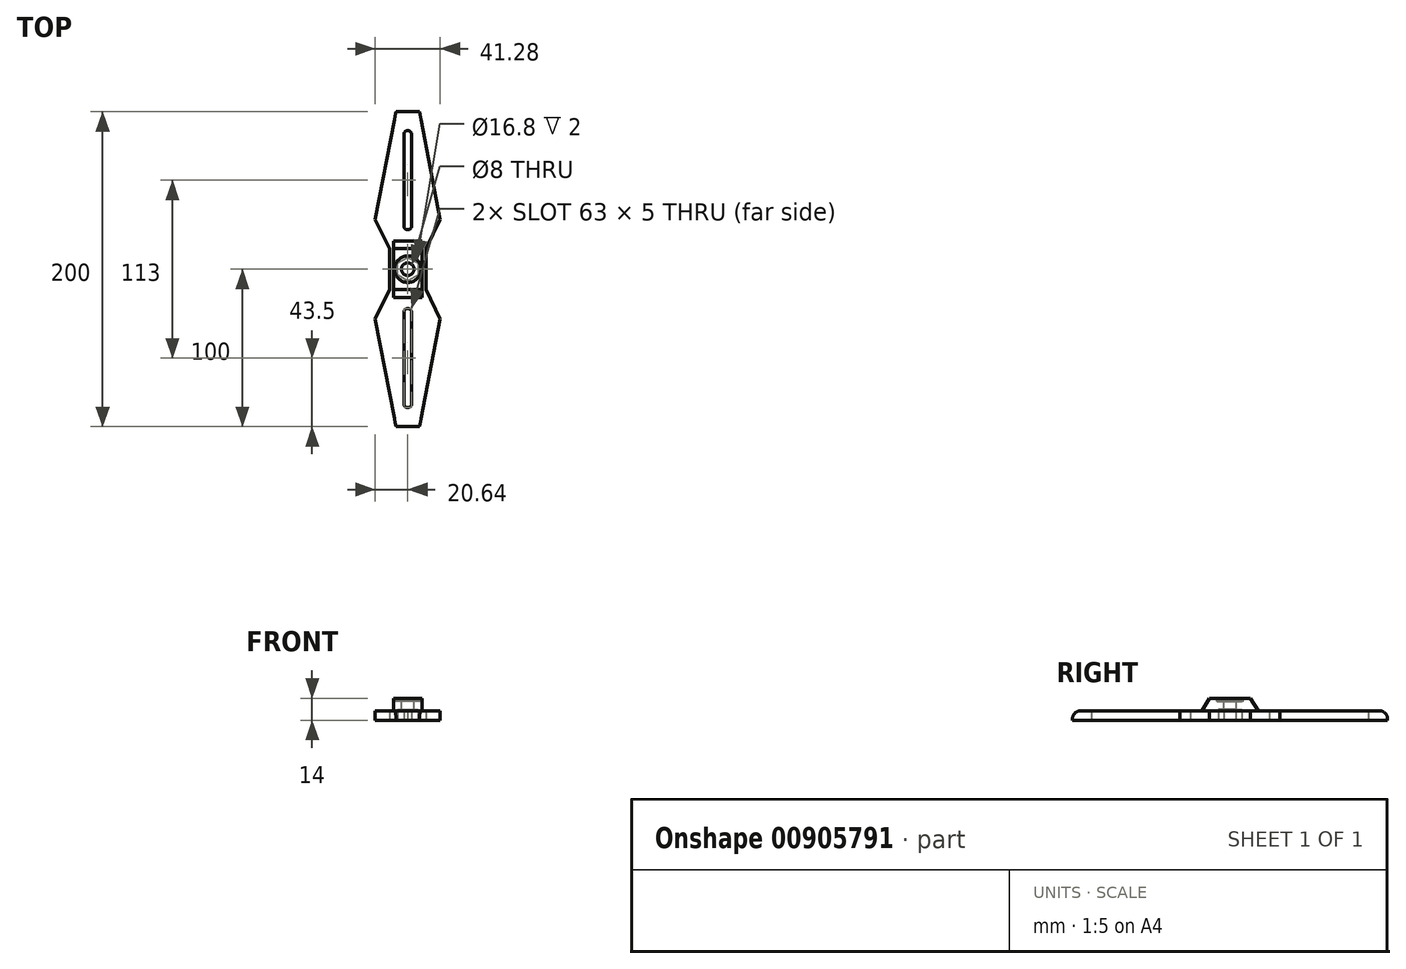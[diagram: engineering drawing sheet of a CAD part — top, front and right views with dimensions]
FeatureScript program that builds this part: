
annotation { "Feature Type Name" : "Feature", "Feature Type Description" : "" }
export const myFeature = defineFeature(function(context is Context, id is Id, definition is map)
    precondition{}
    {
        {
            var Q0;
            Q0=qCreatedBy(makeId("Top.planeOp"),FACE);
            var sketch = newSketch(context, id + "F0", { "sketchPlane" : qUnion([Q0])});
            skLineSegment(sketch, "E0.top", {"start": v(-7.5, 100) * mm, "end": v(7.5, 100) * mm});
            skPoint(sketch, "E0.middle", {"position": v(0, 0) * mm});
            skCircle(sketch, "E1.cCircle", {"center": v(0, 0) * mm, "radius": 7.5 * mm, "construction": true});
            skLineSegment(sketch, "E1.0", {"start": v(0, 7.5) * mm, "end": v(6.5, 3.75) * mm});
            skLineSegment(sketch, "E1.1", {"start": v(6.5, 3.75) * mm, "end": v(6.5, -3.75) * mm});
            skLineSegment(sketch, "E1.2", {"start": v(6.5, -3.75) * mm, "end": v(0, -7.5) * mm});
            skLineSegment(sketch, "E1.3", {"start": v(0, -7.5) * mm, "end": v(-6.5, -3.75) * mm});
            skLineSegment(sketch, "E1.4", {"start": v(-6.5, -3.75) * mm, "end": v(-6.5, 3.75) * mm});
            skLineSegment(sketch, "E1.5", {"start": v(-6.5, 3.75) * mm, "end": v(0, 7.5) * mm});
            skPoint(sketch, "E2.orphan", {"position": v(-12.5, 100) * mm});
            skPoint(sketch, "E3.orphan", {"position": v(12.5, 100) * mm});
            skLineSegment(sketch, "E4.trimOffspring", {"start": v(11.5, -13) * mm, "end": v(11.5, 13) * mm});
            skLineSegment(sketch, "E5.trimOffspring", {"start": v(-11.5, -13) * mm, "end": v(-11.5, 13) * mm});
            skLineSegment(sketch, "E6.bottom", {"start": v(0, -88) * mm, "end": v(0, -88) * mm});
            skLineSegment(sketch, "E6.top", {"start": v(0, 88) * mm, "end": v(0, 88) * mm});
            skLineSegment(sketch, "E6.left", {"start": v(-2.5, 27.5) * mm, "end": v(-2.5, 85.5) * mm});
            skLineSegment(sketch, "E6.right", {"start": v(2.5, 27.5) * mm, "end": v(2.5, 85.5) * mm});
            skPoint(sketch, "E7.visualSharp", {"position": v(-2.5, -88) * mm});
            skArc(sketch, "E7.filletArc", {"start": v(-2.5, -85.5) * mm, "mid": v(-1.77, -87.27) * mm, "end": v(0, -88) * mm});
            skPoint(sketch, "E8.visualSharp", {"position": v(2.5, -88) * mm});
            skArc(sketch, "E8.filletArc", {"start": v(0, -88) * mm, "mid": v(1.77, -87.27) * mm, "end": v(2.5, -85.5) * mm});
            skPoint(sketch, "E9.visualSharp", {"position": v(-2.5, 88) * mm});
            skArc(sketch, "E9.filletArc", {"start": v(0, 88) * mm, "mid": v(-1.77, 87.27) * mm, "end": v(-2.5, 85.5) * mm});
            skPoint(sketch, "E10.visualSharp", {"position": v(2.5, 88) * mm});
            skArc(sketch, "E10.filletArc", {"start": v(2.5, 85.5) * mm, "mid": v(1.77, 87.27) * mm, "end": v(0, 88) * mm});
            skLineSegment(sketch, "E11", {"start": v(0, 25) * mm, "end": v(0, 25) * mm});
            skLineSegment(sketch, "E12", {"start": v(-11.5, 13) * mm, "end": v(11.5, 13) * mm, "construction": true});
            skArc(sketch, "E13.filletArc", {"start": v(0, 25) * mm, "mid": v(1.77, 25.73) * mm, "end": v(2.5, 27.5) * mm});
            skArc(sketch, "E14.filletArc", {"start": v(-2.5, 27.5) * mm, "mid": v(-1.77, 25.73) * mm, "end": v(0, 25) * mm});
            skLineSegment(sketch, "E15.MirrorCS", {"start": v(-2.5, -27.5) * mm, "end": v(-2.5, -85.5) * mm});
            skLineSegment(sketch, "E16.MirrorCS", {"start": v(2.5, -27.5) * mm, "end": v(2.5, -85.5) * mm});
            skArc(sketch, "E17.MirrorCS", {"start": v(-2.5, -27.5) * mm, "mid": v(-1.77, -25.73) * mm, "end": v(0, -25) * mm});
            skArc(sketch, "E18.MirrorCS", {"start": v(0, -25) * mm, "mid": v(1.77, -25.73) * mm, "end": v(2.5, -27.5) * mm});
            skPoint(sketch, "E19.orphan", {"position": v(-25.98, 0) * mm});
            skLineSegment(sketch, "E20", {"start": v(-11.5, 13) * mm, "end": v(-20.64, 31.67) * mm});
            skLineSegment(sketch, "E21", {"start": v(-20.64, 31.67) * mm, "end": v(-7.5, 100) * mm});
            skLineSegment(sketch, "E22.MirrorCS", {"start": v(20.64, 31.67) * mm, "end": v(7.5, 100) * mm});
            skLineSegment(sketch, "E23.MirrorCS", {"start": v(11.5, 13) * mm, "end": v(20.64, 31.67) * mm});
            skLineSegment(sketch, "E24.MirrorCS", {"start": v(-11.5, -13) * mm, "end": v(-20.64, -31.67) * mm});
            skLineSegment(sketch, "E25.MirrorCS", {"start": v(-20.64, -31.67) * mm, "end": v(-7.5, -100) * mm});
            skLineSegment(sketch, "E26.MirrorCS", {"start": v(20.64, -31.67) * mm, "end": v(7.5, -100) * mm});
            skLineSegment(sketch, "E27.MirrorCS", {"start": v(11.5, -13) * mm, "end": v(20.64, -31.67) * mm});
            skLineSegment(sketch, "E28.MirrorCS", {"start": v(-7.5, -100) * mm, "end": v(7.5, -100) * mm});
            skSolve(sketch);
        }
        {
            var Q0;
            Q0=makeQuery(id+"F0.imprint","IMPRINT",FACE,{"disambiguationData":[TD([[makeQuery(id+"F0.imprint","IMPRINT",EDGE,{"derivedFrom":sQuery(id+"F0.wireOp",EDGE,"E0.top")}),-1.0]])]});
            extrude(context, id + "F1", {"entities" : qUnion([Q0]), "depth" : 6 * mm, "offsetDistance" : 25 * mm});
        }
        {
            var Q0;
            Q0=makeQuery(id+"F1.opExtrude","CAP_FACE",FACE,{"disambiguationData":[OSD([sQuery(id+"F0.wireOp",EDGE,"E0.top"),sQuery(id+"F0.wireOp",EDGE,"E1.0"),sQuery(id+"F0.wireOp",EDGE,"E1.1"),sQuery(id+"F0.wireOp",EDGE,"E1.2"),sQuery(id+"F0.wireOp",EDGE,"E1.3"),sQuery(id+"F0.wireOp",EDGE,"E1.4"),sQuery(id+"F0.wireOp",EDGE,"E1.5"),sQuery(id+"F0.wireOp",EDGE,"E4.trimOffspring"),sQuery(id+"F0.wireOp",EDGE,"E5.trimOffspring"),sQuery(id+"F0.wireOp",EDGE,"E6.left"),sQuery(id+"F0.wireOp",EDGE,"E6.right"),sQuery(id+"F0.wireOp",EDGE,"E7.filletArc"),sQuery(id+"F0.wireOp",EDGE,"E8.filletArc"),sQuery(id+"F0.wireOp",EDGE,"E9.filletArc"),sQuery(id+"F0.wireOp",EDGE,"E10.filletArc"),sQuery(id+"F0.wireOp",EDGE,"E13.filletArc"),sQuery(id+"F0.wireOp",EDGE,"E14.filletArc"),sQuery(id+"F0.wireOp",EDGE,"E15.MirrorCS"),sQuery(id+"F0.wireOp",EDGE,"E16.MirrorCS"),sQuery(id+"F0.wireOp",EDGE,"E17.MirrorCS"),sQuery(id+"F0.wireOp",EDGE,"E18.MirrorCS"),sQuery(id+"F0.wireOp",EDGE,"E20"),sQuery(id+"F0.wireOp",EDGE,"E21"),sQuery(id+"F0.wireOp",EDGE,"E22.MirrorCS"),sQuery(id+"F0.wireOp",EDGE,"E23.MirrorCS"),sQuery(id+"F0.wireOp",EDGE,"E24.MirrorCS"),sQuery(id+"F0.wireOp",EDGE,"E25.MirrorCS"),sQuery(id+"F0.wireOp",EDGE,"E26.MirrorCS"),sQuery(id+"F0.wireOp",EDGE,"E27.MirrorCS"),sQuery(id+"F0.wireOp",EDGE,"E28.MirrorCS")])],"isStart":false});
            var sketch = newSketch(context, id + "F2", { "sketchPlane" : qUnion([Q0])});
            skLineSegment(sketch, "E29.bottom", {"start": v(-9, -18) * mm, "end": v(9, -18) * mm});
            skLineSegment(sketch, "E29.top", {"start": v(-9, 18) * mm, "end": v(9, 18) * mm});
            skLineSegment(sketch, "E29.left", {"start": v(-9, -18) * mm, "end": v(-9, 18) * mm});
            skLineSegment(sketch, "E29.right", {"start": v(9, -18) * mm, "end": v(9, 18) * mm});
            skPoint(sketch, "E29.middle", {"position": v(0, 0) * mm});
            skSolve(sketch);
        }
        {
            var Q0;
            Q0 = qSketchRegion(id + "F2", true);
            extrude(context, id + "F3", {"entities" : qUnion([Q0]), "operationType" : NewBodyOperationType.ADD, "depth" : 8 * mm, "offsetDistance" : 25 * mm});
        }
        {
            var Q0;
            Q0=makeQuery(id+"F3.opExtrude","CAP_EDGE",EDGE,{"disambiguationData":[OSD([sQuery(id+"F2.wireOp",EDGE,"E29.bottom")])],"isStart":false});
            var Q1;
            Q1=makeQuery(id+"F3.opExtrude","CAP_EDGE",EDGE,{"disambiguationData":[OSD([sQuery(id+"F2.wireOp",EDGE,"E29.top")])],"isStart":false});
            chamfer(context, id + "F4", {"entities" : qUnion([Q0, Q1]), "chamferType" : ChamferType.TWO_OFFSETS, "width1" : 5 * mm, "oppositeDirection" : false, "width2" : 8 * mm, "tangentPropagation" : true});
        }
        {
            var Q0;
            Q0=makeQuery(id+"F3.opExtrude","CAP_FACE",FACE,{"disambiguationData":[OSD([sQuery(id+"F2.wireOp",EDGE,"E29.bottom"),sQuery(id+"F2.wireOp",EDGE,"E29.top"),sQuery(id+"F2.wireOp",EDGE,"E29.left"),sQuery(id+"F2.wireOp",EDGE,"E29.right")])],"isStart":true});
            var sketch = newSketch(context, id + "F5", { "sketchPlane" : qUnion([Q0])});
            skCircle(sketch, "E30.cCircle", {"center": v(0, 0) * mm, "radius": 7.5 * mm, "construction": true});
            skLineSegment(sketch, "E30.0", {"start": v(0, 7.5) * mm, "end": v(6.5, 3.75) * mm});
            skLineSegment(sketch, "E30.1", {"start": v(6.5, 3.75) * mm, "end": v(6.5, -3.75) * mm});
            skLineSegment(sketch, "E30.2", {"start": v(6.5, -3.75) * mm, "end": v(0, -7.5) * mm});
            skLineSegment(sketch, "E30.3", {"start": v(0, -7.5) * mm, "end": v(-6.5, -3.75) * mm});
            skLineSegment(sketch, "E30.4", {"start": v(-6.5, -3.75) * mm, "end": v(-6.5, 3.75) * mm});
            skLineSegment(sketch, "E30.5", {"start": v(-6.5, 3.75) * mm, "end": v(0, 7.5) * mm});
            skSolve(sketch);
        }
        {
            var Q0;
            Q0 = qSketchRegion(id + "F5", true);
            extrude(context, id + "F6", {"entities" : qUnion([Q0]), "operationType" : NewBodyOperationType.REMOVE, "oppositeDirection" : true, "depth" : 1 * mm, "offsetDistance" : 25 * mm});
        }
        {
            var Q0;
            Q0=makeQuery(id+"F3.opExtrude","CAP_FACE",FACE,{"disambiguationData":[OSD([sQuery(id+"F2.wireOp",EDGE,"E29.bottom"),sQuery(id+"F2.wireOp",EDGE,"E29.top"),sQuery(id+"F2.wireOp",EDGE,"E29.left"),sQuery(id+"F2.wireOp",EDGE,"E29.right")])],"isStart":false});
            var sketch = newSketch(context, id + "F7", { "sketchPlane" : qUnion([Q0])});
            skCircle(sketch, "E31.cCircle", {"center": v(0, 0) * mm, "radius": 8.4 * mm});
            skSolve(sketch);
        }
        {
            var Q0;
            Q0=makeQuery(id+"F7.imprint","IMPRINT",FACE,{"disambiguationData":[TD([[makeQuery(id+"F7.imprint","IMPRINT",EDGE,{"derivedFrom":sQuery(id+"F7.wireOp",EDGE,"E31.cCircle")}),1.0]])]});
            extrude(context, id + "F8", {"entities" : qUnion([Q0]), "operationType" : NewBodyOperationType.REMOVE, "oppositeDirection" : true, "depth" : 2 * mm, "offsetDistance" : 25 * mm});
        }
        {
            var Q0;
            Q0=makeQuery(id+"F8.boolean.opBoolean","COPY",FACE,{"derivedFrom":makeQuery(id+"F8.opExtrude","CAP_FACE",FACE,{"disambiguationData":[OSD([sQuery(id+"F7.wireOp",EDGE,"E31.cCircle")])],"isStart":false})});
            var sketch = newSketch(context, id + "F9", { "sketchPlane" : qUnion([Q0])});
            skCircle(sketch, "E32", {"center": v(0, 0) * mm, "radius": 4 * mm});
            skSolve(sketch);
        }
        {
            var Q0;
            Q0 = qSketchRegion(id + "F9", true);
            extrude(context, id + "F10", {"entities" : qUnion([Q0]), "operationType" : NewBodyOperationType.REMOVE, "oppositeDirection" : true, "depth" : 25 * mm, "offsetDistance" : 25 * mm});
        }
        {
            var Q0;
            Q0=makeQuery(id+"F1.opExtrude","CAP_EDGE",EDGE,{"disambiguationData":[OSD([sQuery(id+"F0.wireOp",EDGE,"E28.MirrorCS")])],"isStart":false});
            var Q1;
            Q1=makeQuery(id+"F1.opExtrude","CAP_EDGE",EDGE,{"disambiguationData":[OSD([sQuery(id+"F0.wireOp",EDGE,"E0.top")])],"isStart":false});
            fillet(context, id + "F11", {"entities" : qUnion([Q0, Q1]), "radius" : 5 * mm, "tangentPropagation" : true, "allowEdgeOverflow" : false});
        }
    });
